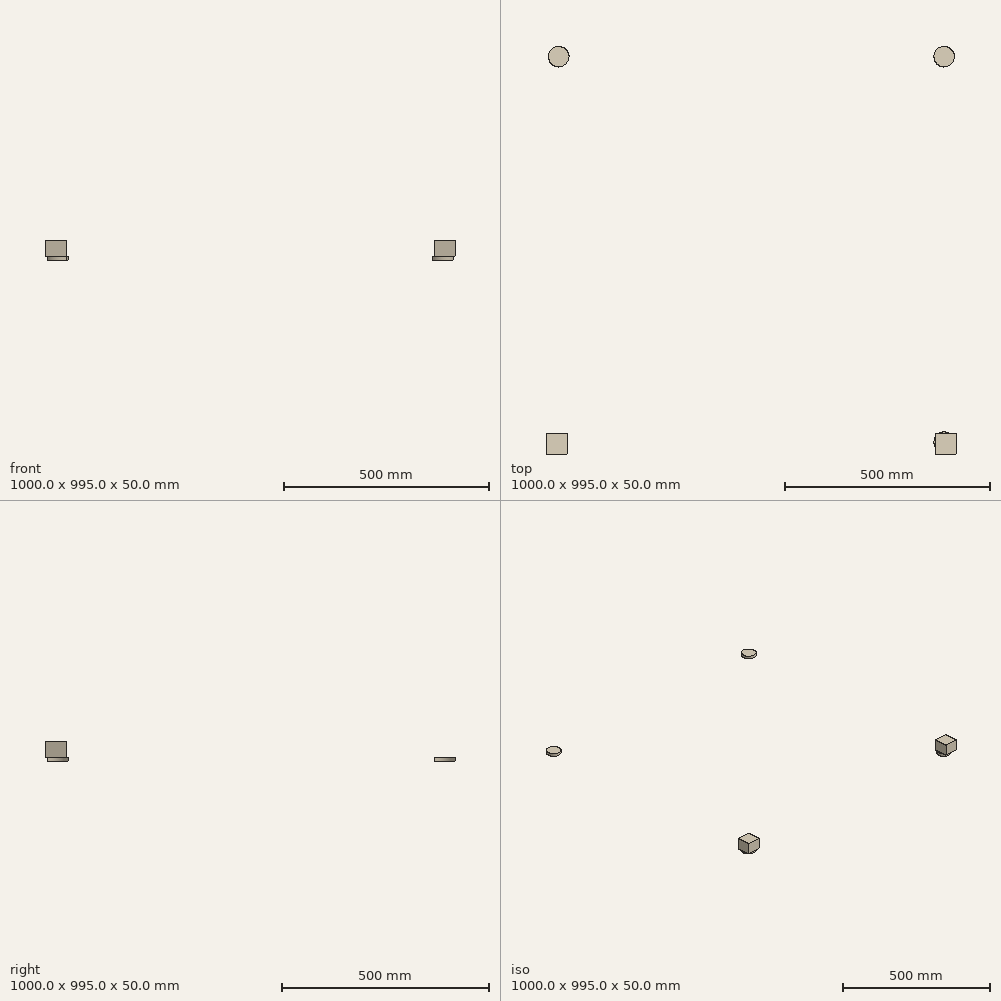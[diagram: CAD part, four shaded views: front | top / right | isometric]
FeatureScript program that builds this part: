
annotation { "Feature Type Name" : "Feature", "Feature Type Description" : "" }
export const myFeature = defineFeature(function(context is Context, id is Id, definition is map)
    precondition{}
    {
        {
            var Q0;
            Q0=qCreatedBy(makeId("Top.planeOp"),FACE);
            var sketch = newSketch(context, id + "F0", { "sketchPlane" : qUnion([Q0])});
            skLineSegment(sketch, "E0.bottom", {"start": v(-500, -500) * mm, "end": v(500, -500) * mm});
            skLineSegment(sketch, "E0.top", {"start": v(-500, 500) * mm, "end": v(500, 500) * mm});
            skLineSegment(sketch, "E0.left", {"start": v(-500, -500) * mm, "end": v(-500, 500) * mm});
            skLineSegment(sketch, "E0.right", {"start": v(500, -500) * mm, "end": v(500, 500) * mm});
            skPoint(sketch, "E0.middle", {"position": v(0, 0) * mm});
            skLineSegment(sketch, "E1.bottom", {"start": v(450, 500) * mm, "end": v(500, 500) * mm});
            skLineSegment(sketch, "E1.top", {"start": v(450, 450) * mm, "end": v(500, 450) * mm});
            skLineSegment(sketch, "E1.left", {"start": v(450, 500) * mm, "end": v(450, 450) * mm});
            skLineSegment(sketch, "E1.right", {"start": v(500, 500) * mm, "end": v(500, 450) * mm});
            skLineSegment(sketch, "E2.bottom", {"start": v(-500, -450) * mm, "end": v(-450, -450) * mm});
            skLineSegment(sketch, "E2.top", {"start": v(-500, -500) * mm, "end": v(-450, -500) * mm});
            skLineSegment(sketch, "E2.left", {"start": v(-500, -450) * mm, "end": v(-500, -500) * mm});
            skLineSegment(sketch, "E2.right", {"start": v(-450, -450) * mm, "end": v(-450, -500) * mm});
            skLineSegment(sketch, "E3.bottom", {"start": v(-500, 500) * mm, "end": v(-450, 500) * mm});
            skLineSegment(sketch, "E3.top", {"start": v(-500, 450) * mm, "end": v(-450, 450) * mm});
            skLineSegment(sketch, "E3.left", {"start": v(-500, 500) * mm, "end": v(-500, 450) * mm});
            skLineSegment(sketch, "E3.right", {"start": v(-450, 500) * mm, "end": v(-450, 450) * mm});
            skLineSegment(sketch, "E4.bottom", {"start": v(450, -450) * mm, "end": v(500, -450) * mm});
            skLineSegment(sketch, "E4.top", {"start": v(450, -500) * mm, "end": v(500, -500) * mm});
            skLineSegment(sketch, "E4.left", {"start": v(450, -450) * mm, "end": v(450, -500) * mm});
            skLineSegment(sketch, "E4.right", {"start": v(500, -450) * mm, "end": v(500, -500) * mm});
            skSolve(sketch);
        }
        {
            var Q0;
            Q0=makeQuery(id+"F0.imprint","IMPRINT",FACE,{"disambiguationData":[TD([[makeQuery(id+"F0.imprint","IMPRINT",EDGE,{"derivedFrom":sQuery(id+"F0.wireOp",EDGE,"E0.bottom")}),1.0]])]});
            var Q1;
            Q1=makeQuery(id+"F0.imprint","IMPRINT",FACE,{"disambiguationData":[TD([[makeQuery(id+"F0.imprint","IMPRINT",EDGE,{"derivedFrom":sQuery(id+"F0.wireOp",EDGE,"E3.bottom")}),-1.0]])]});
            var Q2;
            Q2=makeQuery(id+"F0.imprint","IMPRINT",FACE,{"disambiguationData":[TD([[makeQuery(id+"F0.imprint","IMPRINT",EDGE,{"derivedFrom":sQuery(id+"F0.wireOp",EDGE,"E2.bottom")}),-1.0]])]});
            var Q3;
            Q3=makeQuery(id+"F0.imprint","IMPRINT",FACE,{"disambiguationData":[TD([[makeQuery(id+"F0.imprint","IMPRINT",EDGE,{"derivedFrom":sQuery(id+"F0.wireOp",EDGE,"E4.bottom")}),-1.0]])]});
            var Q4;
            Q4=makeQuery(id+"F0.imprint","IMPRINT",FACE,{"disambiguationData":[TD([[makeQuery(id+"F0.imprint","IMPRINT",EDGE,{"derivedFrom":sQuery(id+"F0.wireOp",EDGE,"E1.bottom")}),-1.0]])]});
            extrude(context, id + "F1", {"entities" : qUnion([Q0, Q1, Q2, Q3, Q4]), "depth" : 25 * mm});
        }
        {
            var Q0;
            Q0=makeQuery(id+"F0.imprint","IMPRINT",FACE,{"disambiguationData":[TD([[makeQuery(id+"F0.imprint","IMPRINT",EDGE,{"derivedFrom":sQuery(id+"F0.wireOp",EDGE,"E3.bottom")}),-1.0]])]});
            var Q1;
            Q1=makeQuery(id+"F0.imprint","IMPRINT",FACE,{"disambiguationData":[TD([[makeQuery(id+"F0.imprint","IMPRINT",EDGE,{"derivedFrom":sQuery(id+"F0.wireOp",EDGE,"E1.bottom")}),-1.0]])]});
            var Q2;
            Q2=makeQuery(id+"F0.imprint","IMPRINT",FACE,{"disambiguationData":[TD([[makeQuery(id+"F0.imprint","IMPRINT",EDGE,{"derivedFrom":sQuery(id+"F0.wireOp",EDGE,"E2.bottom")}),-1.0]])]});
            var Q3;
            Q3=makeQuery(id+"F0.imprint","IMPRINT",FACE,{"disambiguationData":[TD([[makeQuery(id+"F0.imprint","IMPRINT",EDGE,{"derivedFrom":sQuery(id+"F0.wireOp",EDGE,"E4.bottom")}),-1.0]])]});
            extrude(context, id + "F2", {"entities" : qUnion([Q0, Q1, Q2, Q3]), "operationType" : NewBodyOperationType.ADD, "depth" : 40 * mm});
        }
        {
            var Q0;
            Q0=makeQuery(id+"F1.opExtrude","CAP_FACE",FACE,{"disambiguationData":[OSD([sQuery(id+"F0.wireOp",EDGE,"E0.bottom"),sQuery(id+"F0.wireOp",EDGE,"E0.top"),sQuery(id+"F0.wireOp",EDGE,"E0.left"),sQuery(id+"F0.wireOp",EDGE,"E0.right")])],"isStart":true});
            var sketch = newSketch(context, id + "F3", { "sketchPlane" : qUnion([Q0])});
            skCircle(sketch, "E5", {"center": v(-470, 470) * mm, "radius": 25 * mm});
            skCircle(sketch, "E6", {"center": v(470, 470) * mm, "radius": 25 * mm});
            skCircle(sketch, "E7", {"center": v(470, -470) * mm, "radius": 25 * mm});
            skCircle(sketch, "E8", {"center": v(-470, -470) * mm, "radius": 25 * mm});
            skSolve(sketch);
        }
        {
            var Q0;
            Q0=makeQuery(id+"F3.imprint","IMPRINT",FACE,{"disambiguationData":[TD([[makeQuery(id+"F3.imprint","IMPRINT",EDGE,{"derivedFrom":sQuery(id+"F3.wireOp",EDGE,"E5")}),1.0]])]});
            var Q1;
            Q1=makeQuery(id+"F3.imprint","IMPRINT",FACE,{"disambiguationData":[TD([[makeQuery(id+"F3.imprint","IMPRINT",EDGE,{"derivedFrom":sQuery(id+"F3.wireOp",EDGE,"E6")}),1.0]])]});
            var Q2;
            Q2=makeQuery(id+"F3.imprint","IMPRINT",FACE,{"disambiguationData":[TD([[makeQuery(id+"F3.imprint","IMPRINT",EDGE,{"derivedFrom":sQuery(id+"F3.wireOp",EDGE,"E7")}),1.0]])]});
            var Q3;
            Q3=makeQuery(id+"F3.imprint","IMPRINT",FACE,{"disambiguationData":[TD([[makeQuery(id+"F3.imprint","IMPRINT",EDGE,{"derivedFrom":sQuery(id+"F3.wireOp",EDGE,"E8")}),1.0]])]});
            extrude(context, id + "F4", {"entities" : qUnion([Q0, Q1, Q2, Q3]), "operationType" : NewBodyOperationType.ADD, "depth" : 10 * mm});
        }
    });
